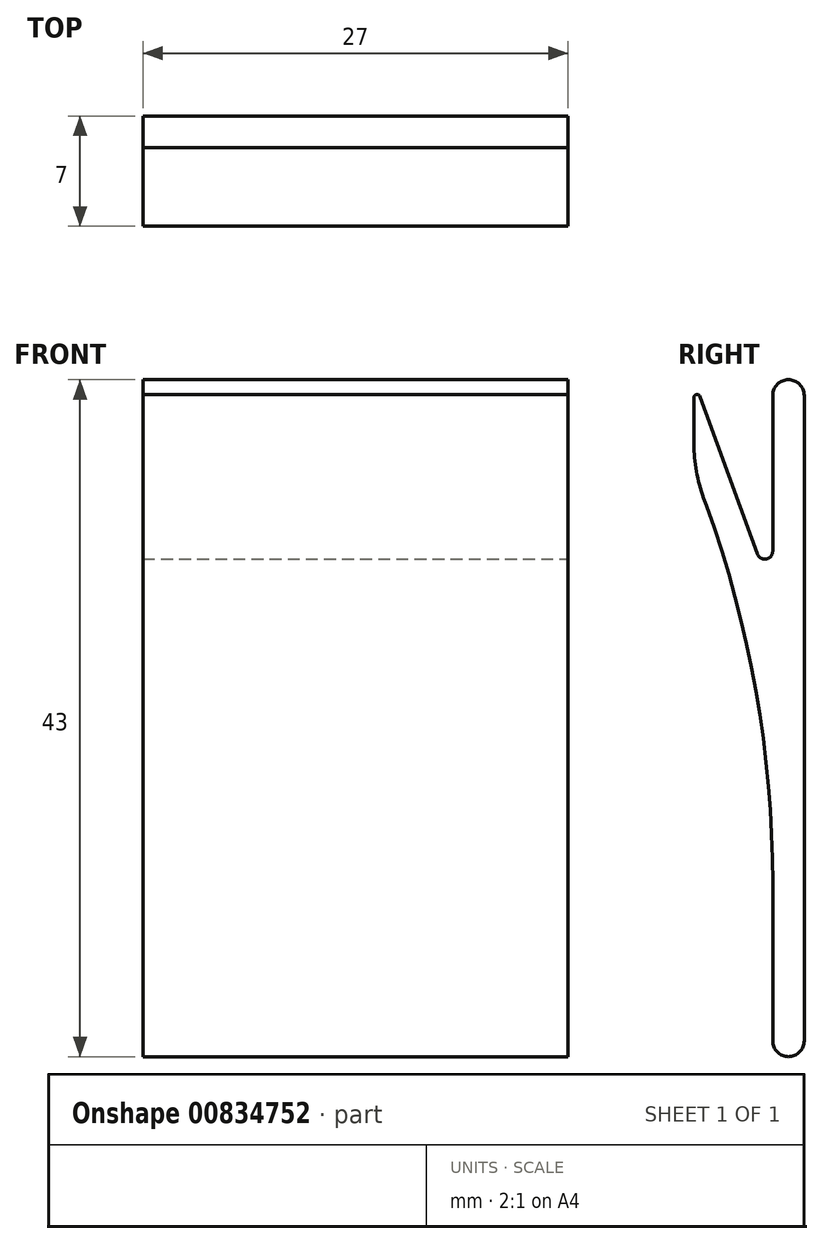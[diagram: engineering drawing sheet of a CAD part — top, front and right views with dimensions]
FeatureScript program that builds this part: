
annotation { "Feature Type Name" : "Feature", "Feature Type Description" : "" }
export const myFeature = defineFeature(function(context is Context, id is Id, definition is map)
    precondition{}
    {
        {
            var Q0;
            Q0=qCreatedBy(makeId("Front.planeOp"),FACE);
            var sketch = newSketch(context, id + "F0", { "sketchPlane" : qUnion([Q0])});
            skLineSegment(sketch, "E0.bottom", {"start": v(0, 0) * mm, "end": v(27, 0) * mm});
            skLineSegment(sketch, "E0.top", {"start": v(0, 43) * mm, "end": v(27, 43) * mm});
            skLineSegment(sketch, "E0.left", {"start": v(0, 0) * mm, "end": v(0, 43) * mm});
            skLineSegment(sketch, "E0.right", {"start": v(27, 0) * mm, "end": v(27, 43) * mm});
            skSolve(sketch);
        }
        {
            var Q0;
            Q0=makeQuery(id+"F0.imprint","IMPRINT",FACE,{"disambiguationData":[TD([[makeQuery(id+"F0.imprint","IMPRINT",EDGE,{"derivedFrom":sQuery(id+"F0.wireOp",EDGE,"E0.bottom")}),1.0]])]});
            extrude(context, id + "F1", {"entities" : qUnion([Q0]), "depth" : 2 * mm, "offsetDistance" : 25 * mm});
        }
        {
            var Q0;
            Q0=qCreatedBy(makeId("Right.planeOp"),FACE);
            var sketch = newSketch(context, id + "F2", { "sketchPlane" : qUnion([Q0])});
            skLineSegment(sketch, "E1", {"start": v(0, 23.77) * mm, "end": v(-7, 43) * mm});
            skLineSegment(sketch, "E2", {"start": v(-7, 43) * mm, "end": v(-7, 37.15) * mm});
            skLineSegment(sketch, "E3", {"start": v(-7, 37.15) * mm, "end": v(0, 17.92) * mm});
            skLineSegment(sketch, "E4", {"start": v(0, 17.92) * mm, "end": v(0, 23.77) * mm});
            skLineSegment(sketch, "E5", {"start": v(-7, 37.15) * mm, "end": v(-5.12, 37.84) * mm, "construction": true});
            skSolve(sketch);
        }
        {
            var Q0;
            Q0 = qSketchRegion(id + "F2", true);
            var Q1;
            Q1=makeQuery(id+"F1.opExtrude","SWEPT_FACE",FACE,{"disambiguationData":[OSD([sQuery(id+"F0.wireOp",EDGE,"E0.right")])]});
            extrude(context, id + "F3", {"entities" : qUnion([Q0]), "operationType" : NewBodyOperationType.ADD, "endBound" : BoundingType.UP_TO_SURFACE, "depth" : 25 * mm, "endBoundEntityFace" : qUnion([Q1]), "offsetDistance" : 25 * mm});
        }
        {
            var Q0;
            Q0=makeQuery(id+"F3.boolean.opBoolean","INTERSECT",EDGE,{"derivedFrom":[makeQuery(id+"F1.opExtrude","CAP_FACE",FACE,{"disambiguationData":[OSD([sQuery(id+"F0.wireOp",EDGE,"E0.bottom"),sQuery(id+"F0.wireOp",EDGE,"E0.top"),sQuery(id+"F0.wireOp",EDGE,"E0.left"),sQuery(id+"F0.wireOp",EDGE,"E0.right")])],"isStart":false}),makeQuery(id+"F3.opExtrude","SWEPT_FACE",FACE,{"disambiguationData":[OSD([sQuery(id+"F2.wireOp",EDGE,"E3")])]})]});
            fillet(context, id + "F4", {"entities" : qUnion([Q0]), "radius" : 70 * mm, "tangentPropagation" : true, "allowEdgeOverflow" : false});
        }
        {
            var Q0;
            Q0=makeQuery(id+"F3.boolean.opBoolean","INTERSECT",EDGE,{"derivedFrom":[makeQuery(id+"F1.opExtrude","CAP_FACE",FACE,{"disambiguationData":[OSD([sQuery(id+"F0.wireOp",EDGE,"E0.bottom"),sQuery(id+"F0.wireOp",EDGE,"E0.top"),sQuery(id+"F0.wireOp",EDGE,"E0.left"),sQuery(id+"F0.wireOp",EDGE,"E0.right")])],"isStart":false}),makeQuery(id+"F3.opExtrude","SWEPT_FACE",FACE,{"disambiguationData":[OSD([sQuery(id+"F2.wireOp",EDGE,"E1")])]})]});
            fillet(context, id + "F5", {"entities" : qUnion([Q0]), "radius" : 0.5 * mm, "tangentPropagation" : true, "allowEdgeOverflow" : false});
        }
        {
            var Q0;
            Q0=makeQuery(id+"F3.opExtrude","SWEPT_EDGE",EDGE,{"disambiguationData":[OSD([sQuery(id+"F2.wireOp",EDGE,"E2"),sQuery(id+"F2.wireOp",EDGE,"E3")])]});
            fillet(context, id + "F6", {"entities" : qUnion([Q0]), "radius" : 10 * mm, "tangentPropagation" : true, "allowEdgeOverflow" : false});
        }
        {
            var Q0;
            Q0=makeQuery(id+"F1.opExtrude","CAP_EDGE",EDGE,{"disambiguationData":[OSD([sQuery(id+"F0.wireOp",EDGE,"E0.top")])],"isStart":false});
            var Q1;
            Q1=makeQuery(id+"F1.opExtrude","CAP_EDGE",EDGE,{"disambiguationData":[OSD([sQuery(id+"F0.wireOp",EDGE,"E0.top")])],"isStart":true});
            var Q2;
            Q2=makeQuery(id+"F1.opExtrude","CAP_EDGE",EDGE,{"disambiguationData":[OSD([sQuery(id+"F0.wireOp",EDGE,"E0.bottom")])],"isStart":false});
            var Q3;
            Q3=makeQuery(id+"F1.opExtrude","CAP_EDGE",EDGE,{"disambiguationData":[OSD([sQuery(id+"F0.wireOp",EDGE,"E0.bottom")])],"isStart":true});
            fillet(context, id + "F7", {"entities" : qUnion([Q0, Q1, Q2, Q3]), "radius" : 1 * mm, "tangentPropagation" : true, "allowEdgeOverflow" : false});
        }
        {
            var Q0;
            Q0=makeQuery(id+"F3.opExtrude","SWEPT_EDGE",EDGE,{"disambiguationData":[OSD([sQuery(id+"F2.wireOp",EDGE,"E1"),sQuery(id+"F2.wireOp",EDGE,"E2")])]});
            fillet(context, id + "F8", {"entities" : qUnion([Q0]), "radius" : 0.2 * mm, "tangentPropagation" : true, "allowEdgeOverflow" : false});
        }
    });
